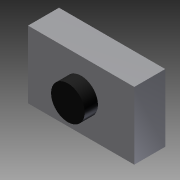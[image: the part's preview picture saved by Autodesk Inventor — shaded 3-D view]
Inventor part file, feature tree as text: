
AUTODESK INVENTOR PART (.ipt)
format: ipt  version: 2012 SP1 (Build 160190100, 190)  size: 85,504 bytes
history: native  units: in
note: dims shown in document units (in); Inventor stores cm internally (conversion verified against a paired STEP export)
features: extrude x2, sketch x2
ambient origin geometry x8: Origin, YZ Plane, XZ Plane, XY Plane, X Axis, Y Axis, Z Axis, Center Point
bodies: Solid1 (feature_tree)
feature tree (4):
  extrude  "Extrusion1"  Depth=0.1496in
  extrude  "Extrusion2"  Depth=0.0295in TaperAngle=0.0deg
  sketch  "Sketch1"  dims[d0=0.2362in d1=0.1496in]
  sketch  "Sketch2"  dims[d2=0.0689in d3=0.0in d5=0.0295in d6=0.0in d9=0.0709in d14=0.0748in]
